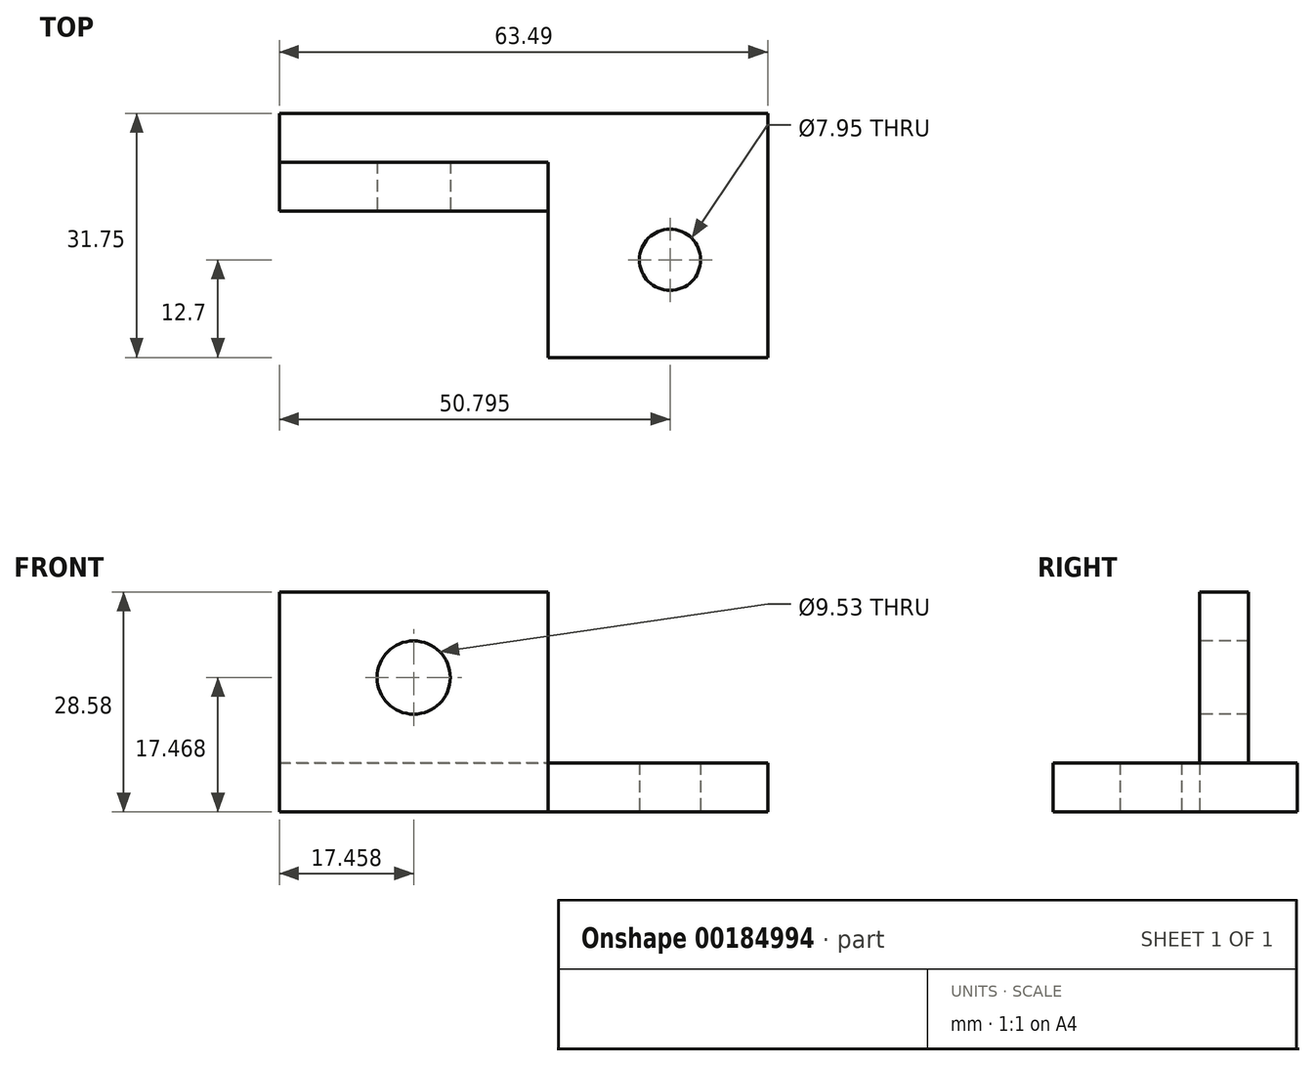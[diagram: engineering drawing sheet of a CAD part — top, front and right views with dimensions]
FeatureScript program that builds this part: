
annotation { "Feature Type Name" : "Feature", "Feature Type Description" : "" }
export const myFeature = defineFeature(function(context is Context, id is Id, definition is map)
    precondition{}
    {
        {
            var Q0;
            Q0=qCreatedBy(makeId("Top.planeOp"),FACE);
            var sketch = newSketch(context, id + "F0", { "sketchPlane" : qUnion([Q0])});
            skLineSegment(sketch, "E0", {"start": v(0, 0) * mm, "end": v(28.57, 0) * mm});
            skLineSegment(sketch, "E1", {"start": v(28.57, 0) * mm, "end": v(28.57, 31.75) * mm});
            skLineSegment(sketch, "E2", {"start": v(28.57, 31.75) * mm, "end": v(-34.92, 31.75) * mm});
            skLineSegment(sketch, "E3", {"start": v(-34.92, 31.75) * mm, "end": v(-34.92, 19.05) * mm});
            skLineSegment(sketch, "E4", {"start": v(-34.92, 19.05) * mm, "end": v(0, 19.05) * mm});
            skLineSegment(sketch, "E5", {"start": v(0, 19.05) * mm, "end": v(0, 0) * mm});
            skCircle(sketch, "E6", {"center": v(15.88, 12.7) * mm, "radius": 3.98 * mm});
            skSolve(sketch);
        }
        {
            var Q0;
            Q0 = qSketchRegion(id + "F0", true);
            extrude(context, id + "F1", {"entities" : qUnion([Q0]), "endBound" : BoundingType.SYMMETRIC, "depth" : 6.35 * mm});
        }
        {
            var Q0;
            Q0=makeQuery(id+"F1.opExtrude","SWEPT_FACE",FACE,{"disambiguationData":[OSD([sQuery(id+"F0.wireOp",EDGE,"E4")])]});
            var sketch = newSketch(context, id + "F2", { "sketchPlane" : qUnion([Q0])});
            skLineSegment(sketch, "E7.bottom", {"start": v(-34.92, 3.18) * mm, "end": v(0, 3.18) * mm});
            skLineSegment(sketch, "E7.top", {"start": v(-34.92, 25.4) * mm, "end": v(0, 25.4) * mm});
            skLineSegment(sketch, "E7.left", {"start": v(-34.92, 3.18) * mm, "end": v(-34.92, 25.4) * mm});
            skLineSegment(sketch, "E7.right", {"start": v(0, 3.18) * mm, "end": v(0, 25.4) * mm});
            skCircle(sketch, "E8", {"center": v(-17.46, 14.29) * mm, "radius": 4.76 * mm});
            skSolve(sketch);
        }
        {
            var Q0;
            Q0 = qSketchRegion(id + "F2", true);
            extrude(context, id + "F3", {"entities" : qUnion([Q0]), "operationType" : NewBodyOperationType.ADD, "oppositeDirection" : true, "depth" : 6.35 * mm});
        }
    });
